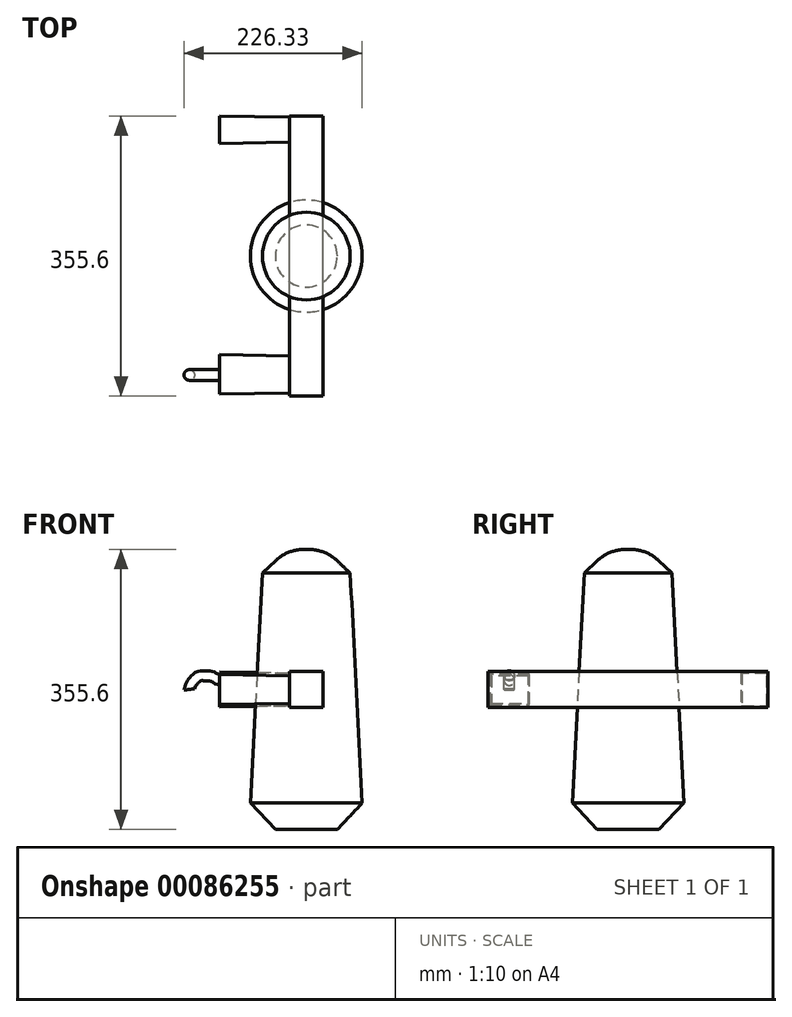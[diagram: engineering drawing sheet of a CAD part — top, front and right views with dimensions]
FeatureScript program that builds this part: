
annotation { "Feature Type Name" : "Feature", "Feature Type Description" : "" }
export const myFeature = defineFeature(function(context is Context, id is Id, definition is map)
    precondition{}
    {
        {
            var Q0;
            Q0=qCreatedBy(makeId("Top.planeOp"),FACE);
            var sketch = newSketch(context, id + "F0", { "sketchPlane" : qUnion([Q0])});
            skCircle(sketch, "E0", {"center": v(0, 0) * mm, "radius": 63.5 * mm});
            skSolve(sketch);
        }
        {
            var Q0;
            Q0=makeQuery(id+"F0.imprint","IMPRINT",FACE,{"disambiguationData":[TD([[makeQuery(id+"F0.imprint","IMPRINT",EDGE,{"derivedFrom":sQuery(id+"F0.wireOp",EDGE,"E0")}),1.0]])]});
            extrude(context, id + "F1", {"entities" : qUnion([Q0]), "depth" : 177.8 * mm, "hasDraft" : true, "draftAngle" : 3 * degree, "draftPullDirection" : true, "hasSecondDirection" : true, "secondDirectionOppositeDirection" : true, "secondDirectionDepth" : 177.8 * mm, "hasSecondDirectionDraft" : true, "secondDirectionDraftAngle" : 3 * degree});
        }
        {
            var Q0;
            {var subQ0=makeQuery(id+"F1.opExtrude","SWEPT_FACE",FACE,{"disambiguationData":[OSD([sQuery(id+"F0.wireOp",EDGE,"E0")])]});Q0=makeQuery(id+"F1.booleanUnion0.opBoolean","MERGE",FACE,{"derivedFrom":[makeQuery(id+"F1.split0.splitOp","SPLIT",FACE,{"derivedFrom":subQ0}),makeQuery(id+"F1.split0.splitOp","SPLIT",FACE,{"derivedFrom":subQ0,"isFromBackBody":true})]});}
            chamfer(context, id + "F2", {"entities" : qUnion([Q0]), "width" : 31.75 * mm, "tangentPropagation" : true});
        }
        {
            var Q0;
            Q0=makeQuery(id+"F1.opExtrude","CAP_FACE",FACE,{"disambiguationData":[OSD([sQuery(id+"F0.wireOp",EDGE,"E0")])],"isStart":false});
            fillet(context, id + "F3", {"entities" : qUnion([Q0]), "radius" : 50.8 * mm, "tangentPropagation" : true, "allowEdgeOverflow" : false});
        }
        {
            var Q0;
            Q0=qCreatedBy(makeId("Front.planeOp"),FACE);
            var sketch = newSketch(context, id + "F4", { "sketchPlane" : qUnion([Q0])});
            skLineSegment(sketch, "E1.bottom", {"start": v(21.48, -23.08) * mm, "end": v(-21.48, -23.08) * mm});
            skLineSegment(sketch, "E1.top", {"start": v(21.48, 23.08) * mm, "end": v(-21.48, 23.08) * mm});
            skLineSegment(sketch, "E1.left", {"start": v(21.48, -23.08) * mm, "end": v(21.48, 23.08) * mm});
            skLineSegment(sketch, "E1.right", {"start": v(-21.48, -23.08) * mm, "end": v(-21.48, 23.08) * mm});
            skPoint(sketch, "E1.middle", {"position": v(0, 0) * mm});
            skSolve(sketch);
        }
        {
            var Q0;
            Q0=makeQuery(id+"F4.imprint","IMPRINT",FACE,{"disambiguationData":[TD([[makeQuery(id+"F4.imprint","IMPRINT",EDGE,{"derivedFrom":sQuery(id+"F4.wireOp",EDGE,"E1.bottom")}),-1.0]])]});
            extrude(context, id + "F5", {"entities" : qUnion([Q0]), "depth" : 177.8 * mm, "hasSecondDirection" : true, "secondDirectionOppositeDirection" : true, "secondDirectionDepth" : 177.8 * mm});
        }
        {
            var Q0;
            Q0=makeQuery(id+"F5.opExtrude","SWEPT_FACE",FACE,{"disambiguationData":[OSD([sQuery(id+"F4.wireOp",EDGE,"E1.bottom")])]});
            cPlane(context, id + "F6", {"entities" : qUnion([Q0]), "cplaneType" : CPlaneType.OFFSET, "offset" : 0.25 * mm, "width" : 152.4 * mm, "height" : 152.4 * mm});
        }
        {
            var Q0;
            Q0=makeQuery(id+"F5.opExtrude","SWEPT_FACE",FACE,{"disambiguationData":[OSD([sQuery(id+"F4.wireOp",EDGE,"E1.right")])]});
            cPlane(context, id + "F7", {"entities" : qUnion([Q0]), "cplaneType" : CPlaneType.OFFSET, "offset" : 0.03 * mm, "width" : 152.4 * mm, "height" : 152.4 * mm});
        }
        {
            var Q0;
            Q0=qCreatedBy(id+"F7.planeOp",FACE);
            var sketch = newSketch(context, id + "F8", { "sketchPlane" : qUnion([Q0])});
            skLineSegment(sketch, "E2.bottom", {"start": v(-144.62, -20.66) * mm, "end": v(-176.22, -20.66) * mm});
            skLineSegment(sketch, "E2.top", {"start": v(-144.62, 20.66) * mm, "end": v(-176.22, 20.66) * mm});
            skLineSegment(sketch, "E2.left", {"start": v(-144.62, -20.66) * mm, "end": v(-144.62, 20.66) * mm});
            skLineSegment(sketch, "E2.right", {"start": v(-176.22, -20.66) * mm, "end": v(-176.22, 20.66) * mm});
            skPoint(sketch, "E2.middle", {"position": v(-160.42, 0) * mm});
            skLineSegment(sketch, "E3.bottom", {"start": v(173.8, -17.42) * mm, "end": v(126.8, -17.42) * mm});
            skLineSegment(sketch, "E3.top", {"start": v(173.8, 17.42) * mm, "end": v(126.8, 17.42) * mm});
            skLineSegment(sketch, "E3.left", {"start": v(173.8, -17.42) * mm, "end": v(173.8, 17.42) * mm});
            skLineSegment(sketch, "E3.right", {"start": v(126.8, -17.42) * mm, "end": v(126.8, 17.42) * mm});
            skPoint(sketch, "E3.middle", {"position": v(150.3, 0) * mm});
            skSolve(sketch);
        }
        {
            var Q0;
            Q0=makeQuery(id+"F8.imprint","IMPRINT",FACE,{"disambiguationData":[TD([[makeQuery(id+"F8.imprint","IMPRINT",EDGE,{"derivedFrom":sQuery(id+"F8.wireOp",EDGE,"E3.bottom")}),-1.0]])]});
            extrude(context, id + "F9", {"entities" : qUnion([Q0]), "depth" : 88.9 * mm, "hasDraft" : true, "draftAngle" : 1 * degree});
        }
        {
            var Q0;
            Q0=makeQuery(id+"F8.imprint","IMPRINT",FACE,{"disambiguationData":[TD([[makeQuery(id+"F8.imprint","IMPRINT",EDGE,{"derivedFrom":sQuery(id+"F8.wireOp",EDGE,"E2.bottom")}),-1.0]])]});
            extrude(context, id + "F10", {"entities" : qUnion([Q0]), "depth" : 88.9 * mm, "hasDraft" : true, "draftAngle" : 1 * degree});
        }
        {
            var Q0;
            Q0=makeQuery(id+"F9.opExtrude","CAP_FACE",FACE,{"disambiguationData":[OSD([sQuery(id+"F8.wireOp",EDGE,"E3.bottom"),sQuery(id+"F8.wireOp",EDGE,"E3.top"),sQuery(id+"F8.wireOp",EDGE,"E3.left"),sQuery(id+"F8.wireOp",EDGE,"E3.right")])],"isStart":false});
            var sketch = newSketch(context, id + "F11", { "sketchPlane" : qUnion([Q0])});
            skCircle(sketch, "E4", {"center": v(151.12, 11.97) * mm, "radius": 6.74 * mm});
            skCircle(sketch, "E5", {"center": v(150.73, -13.8) * mm, "radius": 5.17 * mm});
            skSolve(sketch);
        }
        {
            var Q0;
            Q0=makeQuery(id+"F11.imprint","IMPRINT",FACE,{"disambiguationData":[TD([[makeQuery(id+"F11.imprint","IMPRINT",EDGE,{"derivedFrom":sQuery(id+"F11.wireOp",EDGE,"E4")}),-1.0]])]});
            cPlane(context, id + "F12", {"entities" : qUnion([Q0]), "cplaneType" : CPlaneType.OFFSET, "offset" : 25.4 * mm, "width" : 152.4 * mm, "height" : 152.4 * mm});
        }
        {
            var Q0;
            Q0=qCreatedBy(id+"F12.planeOp",FACE);
            cPlane(context, id + "F13", {"entities" : qUnion([Q0]), "cplaneType" : CPlaneType.OFFSET, "offset" : 12.7 * mm, "width" : 152.4 * mm, "height" : 152.4 * mm});
        }
        {
            var Q0;
            Q0=qCreatedBy(makeId("Front.planeOp"),FACE);
            cPlane(context, id + "F14", {"entities" : qUnion([Q0]), "cplaneType" : CPlaneType.OFFSET, "offset" : 152.4 * mm, "width" : 152.4 * mm, "height" : 152.4 * mm});
        }
        {
            var Q0;
            Q0=qCreatedBy(id+"F14.planeOp",FACE);
            var sketch = newSketch(context, id + "F15", { "sketchPlane" : qUnion([Q0])});
            skFitSpline(sketch, "E6", {"points": [v(-110.47, 11.82) * mm, v(-115.45, 14.03) * mm, v(-118.77, 15.8) * mm, v(-124.69, 16.96) * mm, v(-130.1, 16.96) * mm, v(-135.75, 16.58) * mm, v(-140.57, 13.42) * mm, v(-144.05, 9.55) * mm, v(-146.76, 5.13) * mm, v(-148.42, 0) * mm], "startDerivative": vector(-47.75, 19.42) * mm, "endDerivative": vector(-12.51, -46.9) * mm});
            skSolve(sketch);
        }
        {
            var Q0;
            Q0=makeQuery(id+"F11.imprint","IMPRINT",FACE,{"disambiguationData":[TD([[makeQuery(id+"F11.imprint","IMPRINT",EDGE,{"derivedFrom":sQuery(id+"F11.wireOp",EDGE,"E4")}),1.0]])]});
            var Q1;
            Q1=sQuery(id+"F15.wireOp",EDGE,"E6");
            sweep(context, id + "F16", {"operationType" : NewBodyOperationType.ADD, "profiles" : qUnion([Q0]), "path" : qUnion([Q1])});
        }
    });
